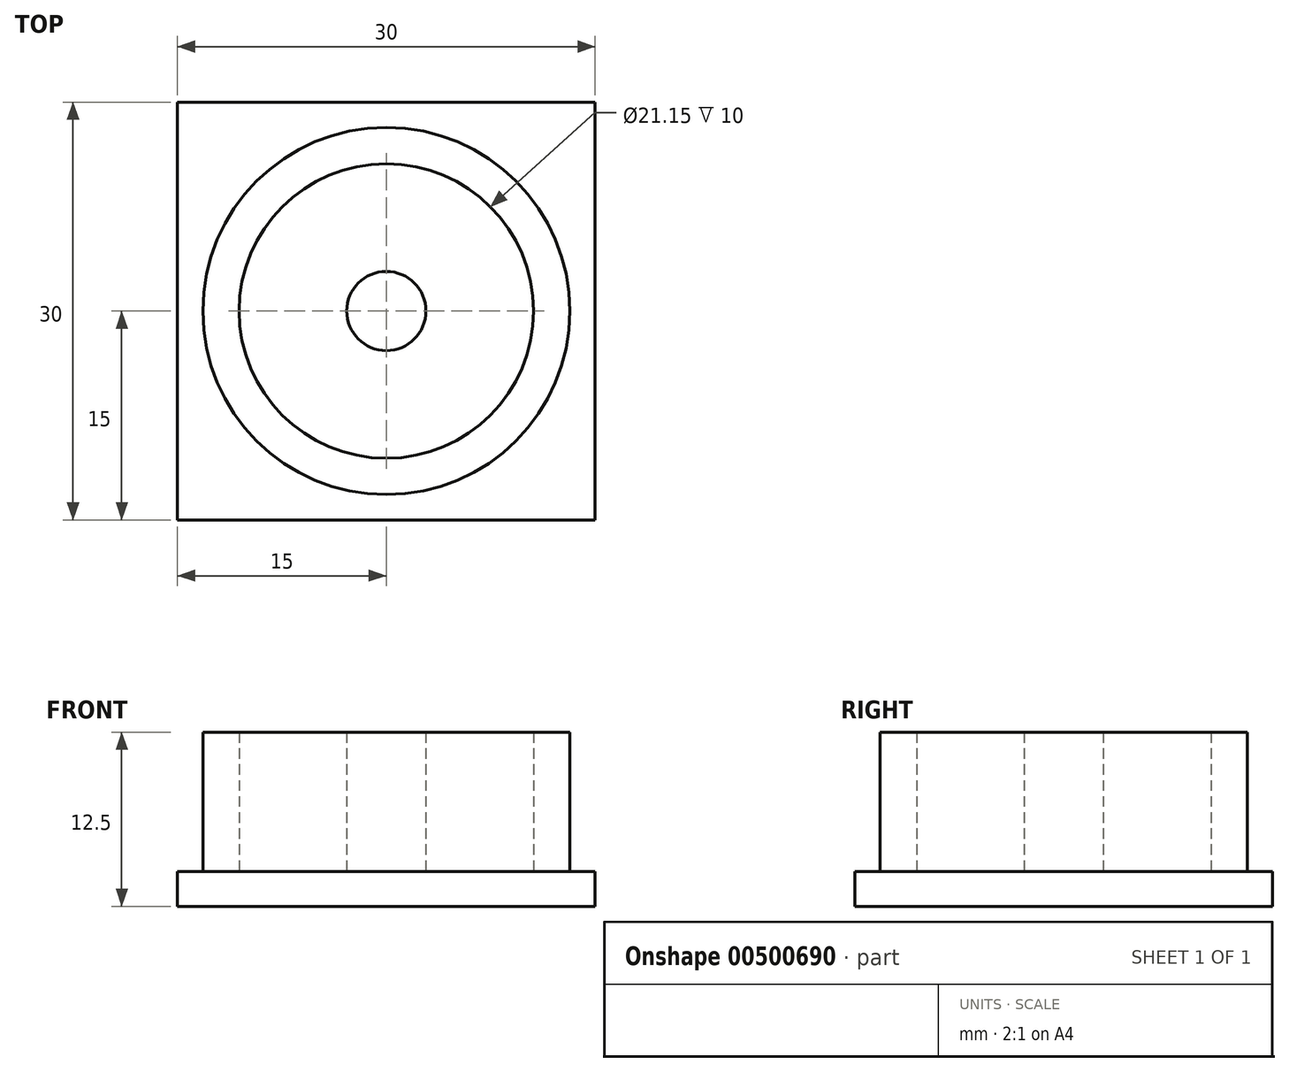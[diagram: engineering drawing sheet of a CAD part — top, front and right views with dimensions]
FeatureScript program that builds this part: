
annotation { "Feature Type Name" : "Feature", "Feature Type Description" : "" }
export const myFeature = defineFeature(function(context is Context, id is Id, definition is map)
    precondition{}
    {
        {
            var Q0;
            Q0=qCreatedBy(makeId("Top.planeOp"),FACE);
            var sketch = newSketch(context, id + "F0", { "sketchPlane" : qUnion([Q0])});
            skLineSegment(sketch, "E0.bottom", {"start": v(-15, 15) * mm, "end": v(15, 15) * mm});
            skLineSegment(sketch, "E0.top", {"start": v(-15, -15) * mm, "end": v(15, -15) * mm});
            skLineSegment(sketch, "E0.left", {"start": v(-15, 15) * mm, "end": v(-15, -15) * mm});
            skLineSegment(sketch, "E0.right", {"start": v(15, 15) * mm, "end": v(15, -15) * mm});
            skPoint(sketch, "E0.middle", {"position": v(0, 0) * mm});
            skSolve(sketch);
        }
        {
            var Q0;
            Q0=makeQuery(id+"F0.imprint","IMPRINT",FACE,{"disambiguationData":[TD([[makeQuery(id+"F0.imprint","IMPRINT",EDGE,{"derivedFrom":sQuery(id+"F0.wireOp",EDGE,"E0.bottom")}),-1.0]])]});
            extrude(context, id + "F1", {"entities" : qUnion([Q0]), "depth" : 2.5 * mm, "offsetDistance" : 25 * mm});
        }
        {
            var Q0;
            Q0=qCreatedBy(makeId("Top.planeOp"),FACE);
            var sketch = newSketch(context, id + "F2", { "sketchPlane" : qUnion([Q0])});
            skCircle(sketch, "E1", {"center": v(0, 0) * mm, "radius": 2.85 * mm});
            skSolve(sketch);
        }
        {
            var Q0;
            Q0 = qSketchRegion(id + "F2", true);
            var Q1;
            Q1 = qSketchRegion(id + "F4", true);
            extrude(context, id + "F3", {"entities" : qUnion([Q0, Q1]), "operationType" : NewBodyOperationType.ADD, "depth" : 12.5 * mm, "offsetDistance" : 25 * mm});
        }
        {
            var Q0;
            Q0=qCreatedBy(makeId("Top.planeOp"),FACE);
            var sketch = newSketch(context, id + "F4", { "sketchPlane" : qUnion([Q0])});
            skCircle(sketch, "E2", {"center": v(0, 0) * mm, "radius": 10.58 * mm});
            skCircle(sketch, "E3", {"center": v(0, 0) * mm, "radius": 13.19 * mm});
            skSolve(sketch);
        }
        {
            var Q0;
            Q0 = qSketchRegion(id + "F4", true);
            extrude(context, id + "F5", {"entities" : qUnion([Q0]), "operationType" : NewBodyOperationType.ADD, "depth" : 12.5 * mm, "offsetDistance" : 25 * mm});
        }
    });
